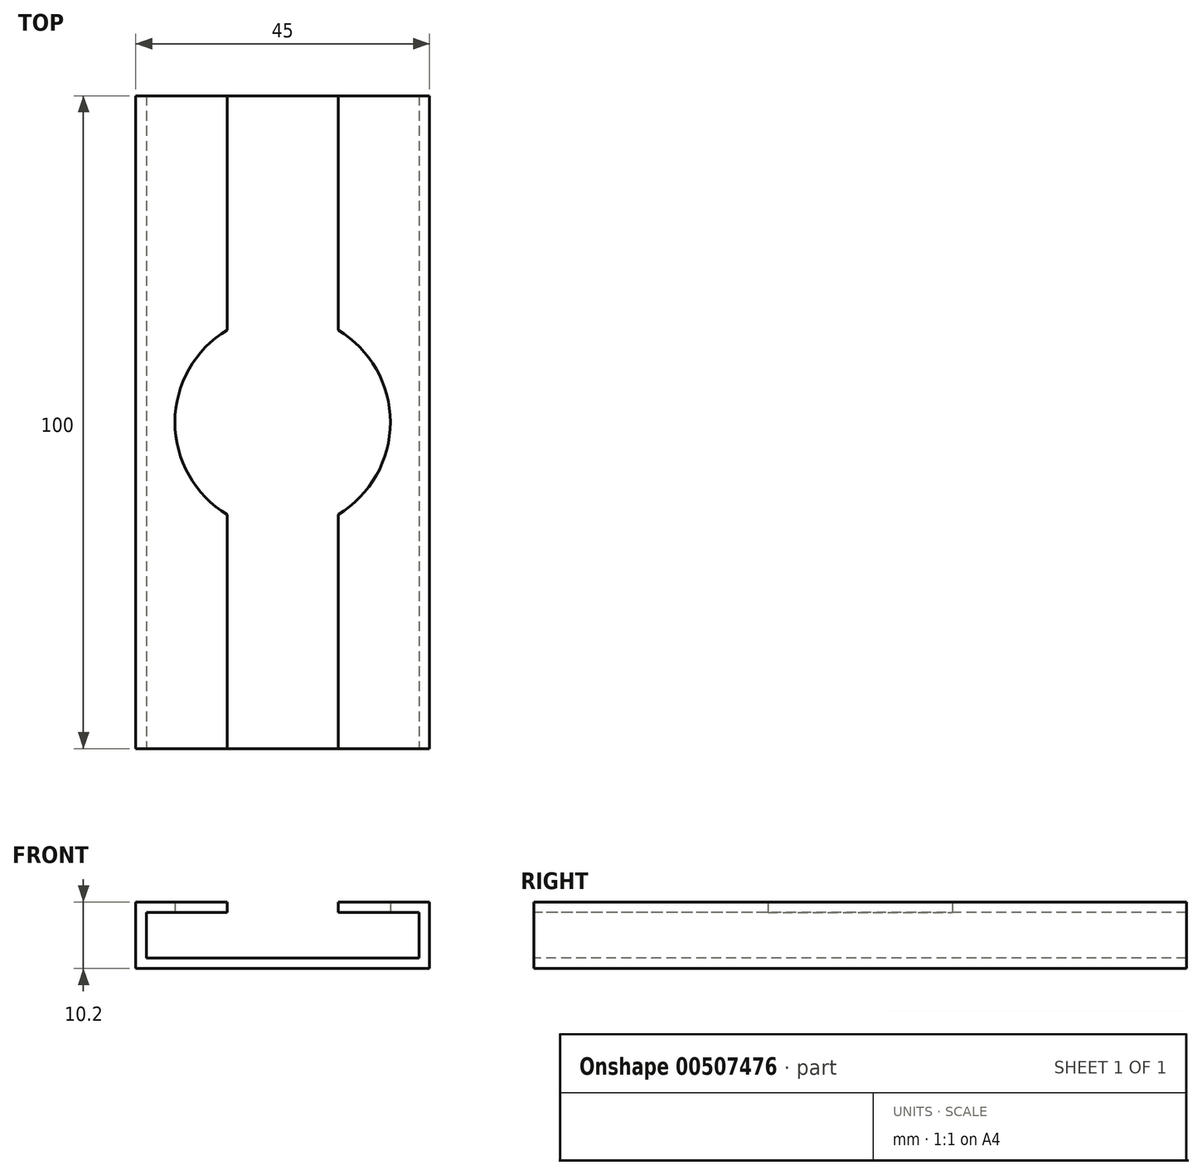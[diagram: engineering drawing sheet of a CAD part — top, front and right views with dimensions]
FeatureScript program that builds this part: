
annotation { "Feature Type Name" : "Feature", "Feature Type Description" : "" }
export const myFeature = defineFeature(function(context is Context, id is Id, definition is map)
    precondition{}
    {
        {
            var Q0;
            Q0=qCreatedBy(makeId("Top.planeOp"),FACE);
            var sketch = newSketch(context, id + "F0", { "sketchPlane" : qUnion([Q0])});
            skLineSegment(sketch, "E0.bottom", {"start": v(-56.34, 35.2) * mm, "end": v(-11.34, 35.2) * mm});
            skLineSegment(sketch, "E0.top", {"start": v(-56.34, -64.8) * mm, "end": v(-11.34, -64.8) * mm});
            skLineSegment(sketch, "E0.left", {"start": v(-56.34, 35.2) * mm, "end": v(-56.34, -64.8) * mm});
            skLineSegment(sketch, "E0.right", {"start": v(-11.34, 35.2) * mm, "end": v(-11.34, -64.8) * mm});
            skSolve(sketch);
        }
        {
            var Q0;
            Q0=makeQuery(id+"F0.imprint","IMPRINT",FACE,{"disambiguationData":[TD([[makeQuery(id+"F0.imprint","IMPRINT",EDGE,{"derivedFrom":sQuery(id+"F0.wireOp",EDGE,"E0.bottom")}),-1.0]])]});
            extrude(context, id + "F1", {"entities" : qUnion([Q0]), "depth" : 10.2 * mm});
        }
        {
            var Q0;
            Q0=makeQuery(id+"F1.opExtrude","CAP_FACE",FACE,{"disambiguationData":[OSD([sQuery(id+"F0.wireOp",EDGE,"E0.bottom"),sQuery(id+"F0.wireOp",EDGE,"E0.top"),sQuery(id+"F0.wireOp",EDGE,"E0.left"),sQuery(id+"F0.wireOp",EDGE,"E0.right")])],"isStart":false});
            var sketch = newSketch(context, id + "F2", { "sketchPlane" : qUnion([Q0])});
            skLineSegment(sketch, "E1.bottom", {"start": v(-42.34, -64.8) * mm, "end": v(-25.34, -64.8) * mm});
            skLineSegment(sketch, "E1.top", {"start": v(-42.34, 35.2) * mm, "end": v(-25.34, 35.2) * mm});
            skLineSegment(sketch, "E1.left", {"start": v(-42.34, -64.8) * mm, "end": v(-42.34, 35.2) * mm});
            skLineSegment(sketch, "E1.right", {"start": v(-25.34, -64.8) * mm, "end": v(-25.34, 35.2) * mm});
            skSolve(sketch);
        }
        {
            var Q0;
            Q0=qSketchRegion(id+"F2",true);
            extrude(context, id + "F3", {"entities" : qUnion([Q0]), "operationType" : NewBodyOperationType.REMOVE, "oppositeDirection" : true, "depth" : 8.6 * mm});
        }
        {
            var Q0;
            Q0=qCreatedBy(makeId("Top.planeOp"),FACE);
            var sketch = newSketch(context, id + "F4", { "sketchPlane" : qUnion([Q0])});
            skLineSegment(sketch, "E2.bottom", {"start": v(-56.34, 35.2) * mm, "end": v(-14.54, 35.2) * mm});
            skLineSegment(sketch, "E2.top", {"start": v(-56.34, -64.8) * mm, "end": v(-14.54, -64.8) * mm});
            skLineSegment(sketch, "E2.left", {"start": v(-56.34, 35.2) * mm, "end": v(-56.34, -64.8) * mm});
            skLineSegment(sketch, "E2.right", {"start": v(-14.54, 35.2) * mm, "end": v(-14.54, -64.8) * mm});
            skSolve(sketch);
        }
        {
            var Q0;
            Q0=makeQuery(id+"F4.imprint","IMPRINT",FACE,{"disambiguationData":[TD([[makeQuery(id+"F4.imprint","IMPRINT",EDGE,{"derivedFrom":sQuery(id+"F4.wireOp",EDGE,"E2.bottom")}),-1.0]])]});
            extrude(context, id + "F5", {"entities" : qUnion([Q0]), "depth" : 7 * mm});
        }
        {
            var Q0;
            Q0=makeQuery(id+"F5.opExtrude","SWEPT_BODY",BODY,{"disambiguationData":[OSD([sQuery(id+"F4.wireOp",EDGE,"E2.bottom"),sQuery(id+"F4.wireOp",EDGE,"E2.top"),sQuery(id+"F4.wireOp",EDGE,"E2.left"),sQuery(id+"F4.wireOp",EDGE,"E2.right")])]});
            transform(context, id + "F6", {"entities" : qUnion([Q0]), "transformType" : TransformType.TRANSLATION_3D, "dx" : 1.6 * mm, "dy" : 0 * mm, "dz" : 1.6 * mm, "makeCopy" : false});
        }
        {
            var Q0;
            Q0=makeQuery(id+"F5.opExtrude","SWEPT_BODY",BODY,{"disambiguationData":[OSD([sQuery(id+"F4.wireOp",EDGE,"E2.bottom"),sQuery(id+"F4.wireOp",EDGE,"E2.top"),sQuery(id+"F4.wireOp",EDGE,"E2.left"),sQuery(id+"F4.wireOp",EDGE,"E2.right")])]});
            var Q1;
            Q1=makeQuery(id+"F1.opExtrude","SWEPT_BODY",BODY,{"disambiguationData":[OSD([sQuery(id+"F0.wireOp",EDGE,"E0.bottom"),sQuery(id+"F0.wireOp",EDGE,"E0.top"),sQuery(id+"F0.wireOp",EDGE,"E0.left"),sQuery(id+"F0.wireOp",EDGE,"E0.right")])]});
            booleanBodies(context, id + "F7", {"operationType" : BooleanOperationType.SUBTRACTION, "tools" : qUnion([Q0]), "targets" : qUnion([Q1])});
        }
        {
            var Q0;
            Q0=qCreatedBy(makeId("Top.planeOp"),FACE);
            var sketch = newSketch(context, id + "F8", { "sketchPlane" : qUnion([Q0])});
            skCircle(sketch, "E3", {"center": v(-33.84, -64.8) * mm, "radius": 16.5 * mm});
            skSolve(sketch);
        }
        {
            var Q0;
            Q0=makeQuery(id+"F8.imprint","IMPRINT",FACE,{"disambiguationData":[TD([[makeQuery(id+"F8.imprint","IMPRINT",EDGE,{"derivedFrom":sQuery(id+"F8.wireOp",EDGE,"E3")}),1.0]])]});
            extrude(context, id + "F9", {"entities" : qUnion([Q0]), "depth" : 10 * mm});
        }
        {
            var Q0;
            Q0=makeQuery(id+"F9.opExtrude","SWEPT_BODY",BODY,{"disambiguationData":[OSD([sQuery(id+"F8.wireOp",EDGE,"E3")])]});
            transform(context, id + "F10", {"entities" : qUnion([Q0]), "transformType" : TransformType.TRANSLATION_3D, "dx" : 0 * mm, "dy" : 50 * mm, "dz" : 4 * mm, "makeCopy" : false});
        }
        {
            var Q0;
            Q0=makeQuery(id+"F9.opExtrude","SWEPT_BODY",BODY,{"disambiguationData":[OSD([sQuery(id+"F8.wireOp",EDGE,"E3")])]});
            var Q1;
            Q1=makeQuery(id+"F1.opExtrude","SWEPT_BODY",BODY,{"disambiguationData":[OSD([sQuery(id+"F0.wireOp",EDGE,"E0.bottom"),sQuery(id+"F0.wireOp",EDGE,"E0.top"),sQuery(id+"F0.wireOp",EDGE,"E0.left"),sQuery(id+"F0.wireOp",EDGE,"E0.right")])]});
            booleanBodies(context, id + "F11", {"operationType" : BooleanOperationType.SUBTRACTION, "tools" : qUnion([Q0]), "targets" : qUnion([Q1])});
        }
    });
